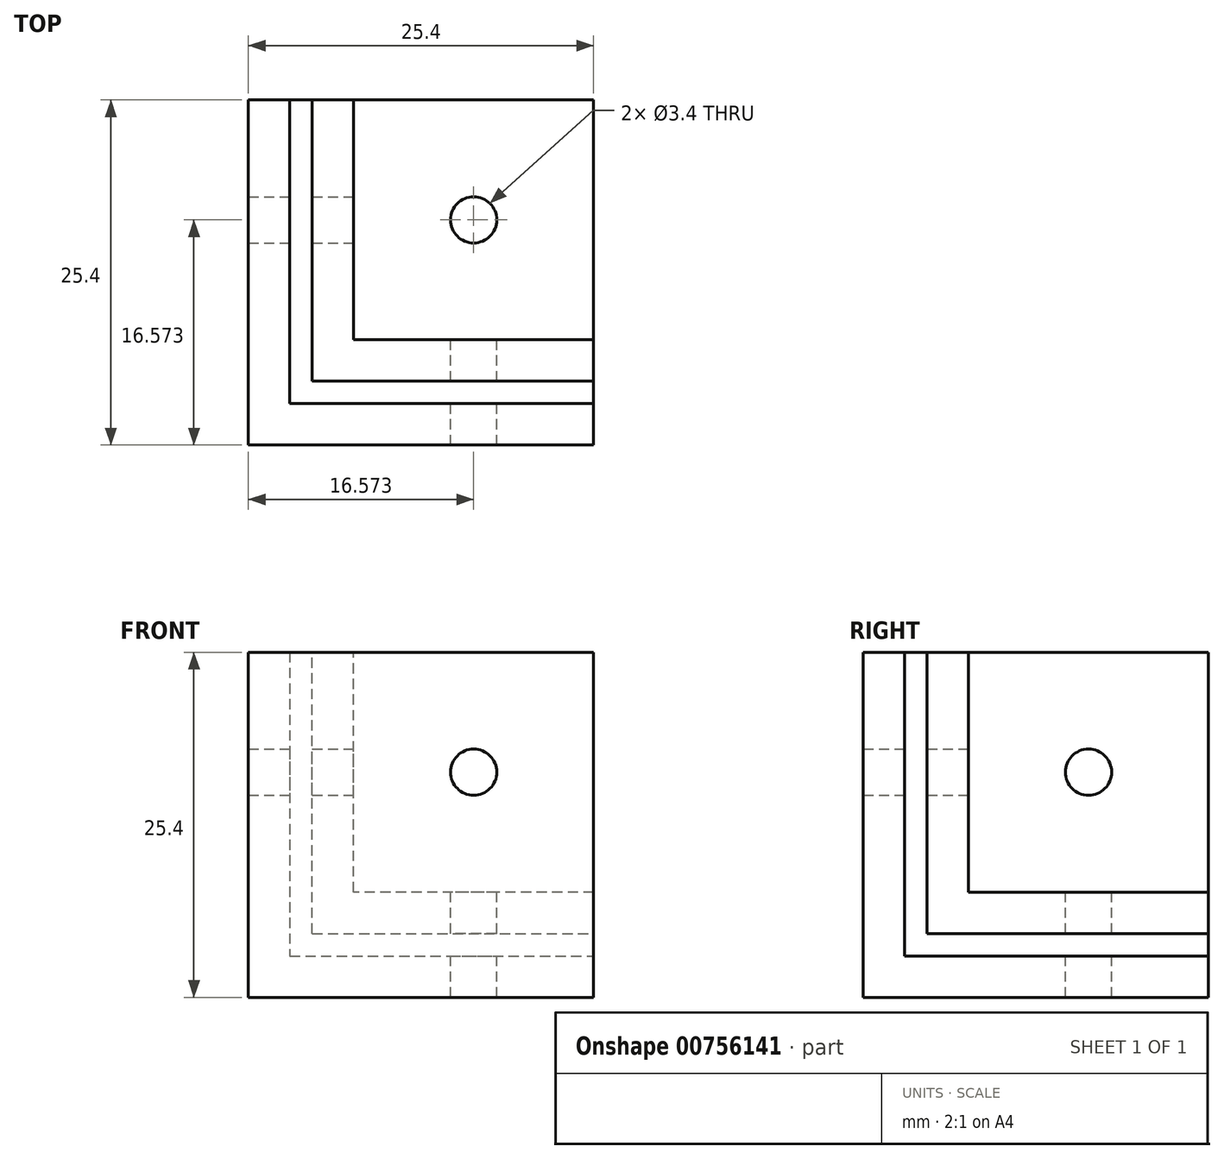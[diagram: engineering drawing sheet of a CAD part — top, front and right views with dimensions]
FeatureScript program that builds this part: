
annotation { "Feature Type Name" : "Feature", "Feature Type Description" : "" }
export const myFeature = defineFeature(function(context is Context, id is Id, definition is map)
    precondition{}
    {
        {
            var Q0;
            Q0=qCreatedBy(makeId("Front.planeOp"),FACE);
            var sketch = newSketch(context, id + "F0", { "sketchPlane" : qUnion([Q0])});
            skLineSegment(sketch, "E0.left", {"start": v(0, 0) * mm, "end": v(0, 0) * mm});
            skLineSegment(sketch, "E1.bottom", {"start": v(0, 0) * mm, "end": v(25.4, 0) * mm});
            skLineSegment(sketch, "E1.top", {"start": v(0, 25.4) * mm, "end": v(25.4, 25.4) * mm});
            skLineSegment(sketch, "E1.left", {"start": v(0, 0) * mm, "end": v(0, 25.4) * mm});
            skLineSegment(sketch, "E1.right", {"start": v(25.4, 0) * mm, "end": v(25.4, 25.4) * mm});
            skSolve(sketch);
        }
        {
            var Q0;
            Q0 = qSketchRegion(id + "F0", true);
            extrude(context, id + "F1", {"entities" : qUnion([Q0]), "depth" : 25.4 * mm, "offsetDistance" : 25.4 * mm});
        }
        {
            var Q0;
            Q0=makeQuery(id+"F1.opExtrude","CAP_FACE",FACE,{"disambiguationData":[OSD([sQuery(id+"F0.wireOp",EDGE,"E1.bottom"),sQuery(id+"F0.wireOp",EDGE,"E1.top"),sQuery(id+"F0.wireOp",EDGE,"E1.left"),sQuery(id+"F0.wireOp",EDGE,"E1.right")])],"isStart":false});
            var sketch = newSketch(context, id + "F2", { "sketchPlane" : qUnion([Q0])});
            skLineSegment(sketch, "E2", {"start": v(3.05, 3.05) * mm, "end": v(22.35, 3.05) * mm});
            skLineSegment(sketch, "E3", {"start": v(22.35, 3.05) * mm, "end": v(22.35, 4.7) * mm});
            skLineSegment(sketch, "E4", {"start": v(22.35, 4.7) * mm, "end": v(4.7, 4.7) * mm});
            skLineSegment(sketch, "E5", {"start": v(4.7, 4.7) * mm, "end": v(4.7, 22.35) * mm});
            skLineSegment(sketch, "E6", {"start": v(4.7, 22.35) * mm, "end": v(3.05, 22.35) * mm});
            skLineSegment(sketch, "E7", {"start": v(3.05, 22.35) * mm, "end": v(3.05, 3.05) * mm});
            skLineSegment(sketch, "E8", {"start": v(12.7, 3.05) * mm, "end": v(12.7, 0) * mm});
            skLineSegment(sketch, "E9", {"start": v(4.7, 22.35) * mm, "end": v(4.7, 25.4) * mm});
            skSolve(sketch);
        }
        {
            var Q0;
            Q0 = qSketchRegion(id + "F2", true);
            extrude(context, id + "F3", {"entities" : qUnion([Q0]), "operationType" : NewBodyOperationType.REMOVE, "oppositeDirection" : true, "depth" : 25.4 * mm, "offsetDistance" : 25.4 * mm});
        }
        {
            var Q0;
            Q0=makeQuery(id+"F1.opExtrude","SWEPT_FACE",FACE,{"disambiguationData":[OSD([sQuery(id+"F0.wireOp",EDGE,"E1.right")])]});
            var sketch = newSketch(context, id + "F4", { "sketchPlane" : qUnion([Q0])});
            skLineSegment(sketch, "E10", {"start": v(-22.35, 3.05) * mm, "end": v(-3.05, 3.05) * mm});
            skLineSegment(sketch, "E11", {"start": v(-3.05, 3.05) * mm, "end": v(-3.05, 4.7) * mm});
            skLineSegment(sketch, "E12", {"start": v(-3.05, 4.7) * mm, "end": v(-20.7, 4.7) * mm});
            skLineSegment(sketch, "E13", {"start": v(-20.7, 4.7) * mm, "end": v(-20.7, 22.35) * mm});
            skLineSegment(sketch, "E14", {"start": v(-20.7, 22.35) * mm, "end": v(-22.35, 22.35) * mm});
            skLineSegment(sketch, "E15", {"start": v(-22.35, 22.35) * mm, "end": v(-22.35, 3.05) * mm});
            skLineSegment(sketch, "E16", {"start": v(-12.7, 3.05) * mm, "end": v(-12.7, 0) * mm});
            skLineSegment(sketch, "E17", {"start": v(-20.7, 22.35) * mm, "end": v(-20.7, 25.4) * mm});
            skPoint(sketch, "E18", {"position": v(-12.7, 0) * mm});
            skSolve(sketch);
        }
        {
            var Q0;
            Q0 = qSketchRegion(id + "F4", true);
            extrude(context, id + "F5", {"entities" : qUnion([Q0]), "operationType" : NewBodyOperationType.REMOVE, "oppositeDirection" : true, "depth" : 25.4 * mm, "offsetDistance" : 25.4 * mm});
        }
        {
            var Q0;
            Q0=makeQuery(id+"F1.opExtrude","SWEPT_FACE",FACE,{"disambiguationData":[OSD([sQuery(id+"F0.wireOp",EDGE,"E1.top")])]});
            var sketch = newSketch(context, id + "F6", { "sketchPlane" : qUnion([Q0])});
            skLineSegment(sketch, "E19", {"start": v(3.05, -22.35) * mm, "end": v(22.35, -22.35) * mm});
            skLineSegment(sketch, "E20", {"start": v(22.35, -22.35) * mm, "end": v(22.35, -20.7) * mm});
            skLineSegment(sketch, "E21", {"start": v(22.35, -20.7) * mm, "end": v(4.7, -20.7) * mm});
            skLineSegment(sketch, "E22", {"start": v(4.7, -20.7) * mm, "end": v(4.7, -3.05) * mm});
            skLineSegment(sketch, "E23", {"start": v(4.7, -3.05) * mm, "end": v(3.05, -3.05) * mm});
            skLineSegment(sketch, "E24", {"start": v(3.05, -3.05) * mm, "end": v(3.05, -22.35) * mm});
            skLineSegment(sketch, "E25", {"start": v(12.7, -22.35) * mm, "end": v(12.7, -25.4) * mm});
            skLineSegment(sketch, "E26", {"start": v(4.7, -3.05) * mm, "end": v(4.7, 0) * mm});
            skSolve(sketch);
        }
        {
            var Q0;
            Q0 = qSketchRegion(id + "F6", true);
            extrude(context, id + "F7", {"entities" : qUnion([Q0]), "operationType" : NewBodyOperationType.REMOVE, "oppositeDirection" : true, "depth" : 25.4 * mm, "offsetDistance" : 25.4 * mm});
        }
        {
            var Q0;
            Q0=makeQuery(id+"F1.opExtrude","CAP_FACE",FACE,{"disambiguationData":[OSD([sQuery(id+"F0.wireOp",EDGE,"E1.bottom"),sQuery(id+"F0.wireOp",EDGE,"E1.top"),sQuery(id+"F0.wireOp",EDGE,"E1.left"),sQuery(id+"F0.wireOp",EDGE,"E1.right")])],"isStart":true});
            var sketch = newSketch(context, id + "F8", { "sketchPlane" : qUnion([Q0])});
            skLineSegment(sketch, "E27.bottom", {"start": v(-3.05, 0) * mm, "end": v(0, 0) * mm});
            skLineSegment(sketch, "E27.top", {"start": v(-3.05, 25.4) * mm, "end": v(0, 25.4) * mm});
            skLineSegment(sketch, "E27.left", {"start": v(-3.05, 0) * mm, "end": v(-3.05, 25.4) * mm});
            skLineSegment(sketch, "E27.right", {"start": v(0, 0) * mm, "end": v(0, 25.4) * mm});
            skLineSegment(sketch, "E28.bottom", {"start": v(0, 0) * mm, "end": v(-25.4, 0) * mm});
            skLineSegment(sketch, "E28.top", {"start": v(0, 3.05) * mm, "end": v(-25.4, 3.05) * mm});
            skLineSegment(sketch, "E28.left", {"start": v(0, 0) * mm, "end": v(0, 3.05) * mm});
            skLineSegment(sketch, "E28.right", {"start": v(-25.4, 0) * mm, "end": v(-25.4, 3.05) * mm});
            skSolve(sketch);
        }
        {
            var Q0;
            Q0 = qSketchRegion(id + "F8", true);
            extrude(context, id + "F9", {"entities" : qUnion([Q0]), "operationType" : NewBodyOperationType.ADD, "oppositeDirection" : true, "depth" : 25.4 * mm, "offsetDistance" : 25.4 * mm});
        }
        {
            var Q0;
            Q0=makeQuery(id+"F1.opExtrude","SWEPT_FACE",FACE,{"disambiguationData":[OSD([sQuery(id+"F0.wireOp",EDGE,"E1.right")])]});
            var sketch = newSketch(context, id + "F10", { "sketchPlane" : qUnion([Q0])});
            skLineSegment(sketch, "E29.bottom", {"start": v(-22.35, 0) * mm, "end": v(-25.4, 0) * mm});
            skLineSegment(sketch, "E29.top", {"start": v(-22.35, 25.4) * mm, "end": v(-25.4, 25.4) * mm});
            skLineSegment(sketch, "E29.left", {"start": v(-22.35, 0) * mm, "end": v(-22.35, 25.4) * mm});
            skLineSegment(sketch, "E29.right", {"start": v(-25.4, 0) * mm, "end": v(-25.4, 25.4) * mm});
            skSolve(sketch);
        }
        {
            var Q0;
            Q0 = qSketchRegion(id + "F10", true);
            extrude(context, id + "F11", {"entities" : qUnion([Q0]), "operationType" : NewBodyOperationType.ADD, "oppositeDirection" : true, "depth" : 25.4 * mm, "offsetDistance" : 25.4 * mm});
        }
        {
            var Q0;
            Q0=makeQuery(id+"F1.opExtrude","SWEPT_FACE",FACE,{"disambiguationData":[OSD([sQuery(id+"F0.wireOp",EDGE,"E1.top")])]});
            var sketch = newSketch(context, id + "F12", { "sketchPlane" : qUnion([Q0])});
            skLineSegment(sketch, "E30.bottom", {"start": v(25.4, 0) * mm, "end": v(7.75, 0) * mm});
            skLineSegment(sketch, "E30.top", {"start": v(25.4, -17.65) * mm, "end": v(7.75, -17.65) * mm});
            skLineSegment(sketch, "E30.left", {"start": v(25.4, 0) * mm, "end": v(25.4, -17.65) * mm});
            skLineSegment(sketch, "E30.right", {"start": v(7.75, 0) * mm, "end": v(7.75, -17.65) * mm});
            skSolve(sketch);
        }
        {
            var Q0;
            Q0 = qSketchRegion(id + "F12", true);
            extrude(context, id + "F13", {"entities" : qUnion([Q0]), "operationType" : NewBodyOperationType.REMOVE, "oppositeDirection" : true, "depth" : 17.65 * mm, "offsetDistance" : 25.4 * mm});
        }
        {
            var Q0;
            Q0=makeQuery(id+"F1.opExtrude","SWEPT_FACE",FACE,{"disambiguationData":[OSD([sQuery(id+"F0.wireOp",EDGE,"E1.top")])]});
            var sketch = newSketch(context, id + "F14", { "sketchPlane" : qUnion([Q0])});
            skLineSegment(sketch, "E31.bottom", {"start": v(3.05, -3.05) * mm, "end": v(4.7, -3.05) * mm});
            skLineSegment(sketch, "E31.top", {"start": v(3.05, 0) * mm, "end": v(4.7, 0) * mm});
            skLineSegment(sketch, "E31.left", {"start": v(3.05, -3.05) * mm, "end": v(3.05, 0) * mm});
            skLineSegment(sketch, "E31.right", {"start": v(4.7, -3.05) * mm, "end": v(4.7, 0) * mm});
            skLineSegment(sketch, "E32.bottom", {"start": v(22.35, -22.35) * mm, "end": v(25.4, -22.35) * mm});
            skLineSegment(sketch, "E32.top", {"start": v(22.35, -20.7) * mm, "end": v(25.4, -20.7) * mm});
            skLineSegment(sketch, "E32.left", {"start": v(22.35, -22.35) * mm, "end": v(22.35, -20.7) * mm});
            skLineSegment(sketch, "E32.right", {"start": v(25.4, -22.35) * mm, "end": v(25.4, -20.7) * mm});
            skSolve(sketch);
        }
        {
            var Q0;
            Q0 = qSketchRegion(id + "F14", true);
            var Q1;
            {var subQ1=makeQuery(id+"F5.opExtrude","SWEPT_FACE",FACE,{"disambiguationData":[OSD([sQuery(id+"F4.wireOp",EDGE,"E10")])]});var subQ4=makeQuery(id+"F3.boolean.opBoolean","COPY",FACE,{"derivedFrom":makeQuery(id+"F3.opExtrude","SWEPT_FACE",FACE,{"disambiguationData":[OSD([sQuery(id+"F2.wireOp",EDGE,"E2")])]})});var subQ5=sQuery(id+"F0.wireOp",EDGE,"E1.left");var subQ9=sQuery(id+"F0.wireOp",EDGE,"E1.right");var subQ10=makeQuery(id+"F1.opExtrude","SWEPT_FACE",FACE,{"disambiguationData":[OSD([subQ9])]});var subQ12=sQuery(id+"F0.wireOp",EDGE,"E1.top");var subQ13=sQuery(id+"F0.wireOp",EDGE,"E1.bottom");var subQ20=makeQuery(id+"F5.boolean.opBoolean","MERGE",FACE,{"derivedFrom":[subQ4,subQ1]});Q1=makeQuery(id+"F9.boolean.opBoolean","MERGE",FACE,{"derivedFrom":[makeQuery(id+"F7.boolean.opBoolean","SPLIT",FACE,{"disambiguationData":[TD([makeQuery(id+"F1.opExtrude","CAP_FACE",FACE,{"disambiguationData":[OSD([subQ13,subQ12,subQ5,subQ9])],"isStart":false})])],"derivedFrom":subQ20}),makeQuery(id+"F7.boolean.opBoolean","SPLIT",FACE,{"disambiguationData":[TD([subQ10])],"derivedFrom":subQ20}),makeQuery(id+"F9.opExtrude","SWEPT_FACE",FACE,{"disambiguationData":[OSD([sQuery(id+"F8.wireOp",EDGE,"E28.top")])]})]});}
            extrude(context, id + "F15", {"entities" : qUnion([Q0]), "operationType" : NewBodyOperationType.REMOVE, "endBound" : BoundingType.UP_TO_SURFACE, "oppositeDirection" : true, "depth" : 25.4 * mm, "endBoundEntityFace" : qUnion([Q1]), "offsetDistance" : 25.4 * mm});
        }
        {
            var Q0;
            Q0=makeQuery(id+"F1.opExtrude","SWEPT_FACE",FACE,{"disambiguationData":[OSD([sQuery(id+"F0.wireOp",EDGE,"E1.right")])]});
            var sketch = newSketch(context, id + "F16", { "sketchPlane" : qUnion([Q0])});
            skLineSegment(sketch, "E33.bottom", {"start": v(-3.05, 4.7) * mm, "end": v(0, 4.7) * mm});
            skLineSegment(sketch, "E33.top", {"start": v(-3.05, 3.05) * mm, "end": v(0, 3.05) * mm});
            skLineSegment(sketch, "E33.left", {"start": v(-3.05, 4.7) * mm, "end": v(-3.05, 3.05) * mm});
            skLineSegment(sketch, "E33.right", {"start": v(0, 4.7) * mm, "end": v(0, 3.05) * mm});
            skSolve(sketch);
        }
        {
            var Q0;
            Q0 = qSketchRegion(id + "F16", true);
            var Q1;
            {var subQ8=makeQuery(id+"F3.boolean.opBoolean","COPY",FACE,{"derivedFrom":makeQuery(id+"F3.opExtrude","SWEPT_FACE",FACE,{"disambiguationData":[OSD([sQuery(id+"F2.wireOp",EDGE,"E7")])]})});Q1=makeQuery(id+"F15.boolean.opBoolean","MERGE",FACE,{"derivedFrom":[makeQuery(id+"F9.boolean.opBoolean","MERGE",FACE,{"derivedFrom":[makeQuery(id+"F5.boolean.opBoolean","SPLIT",FACE,{"disambiguationData":[TD([makeQuery(id+"F5.opExtrude","SWEPT_FACE",FACE,{"disambiguationData":[OSD([sQuery(id+"F4.wireOp",EDGE,"E15")])]})])],"derivedFrom":subQ8}),makeQuery(id+"F7.boolean.opBoolean","MERGE",FACE,{"derivedFrom":[makeQuery(id+"F5.boolean.opBoolean","SPLIT",FACE,{"disambiguationData":[TD([makeQuery(id+"F5.opExtrude","SWEPT_FACE",FACE,{"disambiguationData":[OSD([sQuery(id+"F4.wireOp",EDGE,"E11")])]})])],"derivedFrom":subQ8}),makeQuery(id+"F7.opExtrude","SWEPT_FACE",FACE,{"disambiguationData":[OSD([sQuery(id+"F6.wireOp",EDGE,"E24")])]})]}),makeQuery(id+"F9.opExtrude","SWEPT_FACE",FACE,{"disambiguationData":[OSD([sQuery(id+"F8.wireOp",EDGE,"E27.left")])]})]}),makeQuery(id+"F15.opExtrude","SWEPT_FACE",FACE,{"disambiguationData":[OSD([sQuery(id+"F14.wireOp",EDGE,"E31.left")])]})]});}
            extrude(context, id + "F17", {"entities" : qUnion([Q0]), "operationType" : NewBodyOperationType.REMOVE, "endBound" : BoundingType.UP_TO_SURFACE, "oppositeDirection" : true, "depth" : 25.4 * mm, "endBoundEntityFace" : qUnion([Q1]), "offsetDistance" : 25.4 * mm});
        }
        {
            var Q0;
            Q0=makeQuery(id+"F13.boolean.opBoolean","COPY",FACE,{"derivedFrom":makeQuery(id+"F13.opExtrude","SWEPT_FACE",FACE,{"disambiguationData":[OSD([sQuery(id+"F12.wireOp",EDGE,"E30.top")])]})});
            var sketch = newSketch(context, id + "F18", { "sketchPlane" : qUnion([Q0])});
            skCircle(sketch, "E34", {"center": v(-16.57, 16.57) * mm, "radius": 1.7 * mm});
            skPoint(sketch, "E34.centerSnap0", {"position": v(-25.4, 16.57) * mm});
            skPoint(sketch, "E34.centerSnap1", {"position": v(-16.57, 25.4) * mm});
            skSolve(sketch);
        }
        {
            var Q0;
            Q0 = qSketchRegion(id + "F18", true);
            extrude(context, id + "F19", {"entities" : qUnion([Q0]), "operationType" : NewBodyOperationType.REMOVE, "oppositeDirection" : true, "depth" : 25.4 * mm, "offsetDistance" : 25.4 * mm});
        }
        {
            var Q0;
            Q0=makeQuery(id+"F13.boolean.opBoolean","COPY",FACE,{"derivedFrom":makeQuery(id+"F13.opExtrude","SWEPT_FACE",FACE,{"disambiguationData":[OSD([sQuery(id+"F12.wireOp",EDGE,"E30.right")])]})});
            var sketch = newSketch(context, id + "F20", { "sketchPlane" : qUnion([Q0])});
            skCircle(sketch, "E35", {"center": v(-8.83, 16.57) * mm, "radius": 1.7 * mm});
            skPoint(sketch, "E35.centerSnap0", {"position": v(0, 16.57) * mm});
            skPoint(sketch, "E35.centerSnap1", {"position": v(-8.83, 25.4) * mm});
            skSolve(sketch);
        }
        {
            var Q0;
            Q0=makeQuery(id+"F20.imprint","IMPRINT",FACE,{"disambiguationData":[TD([[makeQuery(id+"F20.imprint","IMPRINT",EDGE,{"derivedFrom":sQuery(id+"F20.wireOp",EDGE,"E35")}),1.0]])]});
            extrude(context, id + "F21", {"entities" : qUnion([Q0]), "operationType" : NewBodyOperationType.REMOVE, "oppositeDirection" : true, "depth" : 25.4 * mm, "offsetDistance" : 25.4 * mm});
        }
        {
            var Q0;
            Q0=makeQuery(id+"F13.boolean.opBoolean","COPY",FACE,{"derivedFrom":makeQuery(id+"F13.opExtrude","CAP_FACE",FACE,{"disambiguationData":[OSD([sQuery(id+"F12.wireOp",EDGE,"E30.bottom"),sQuery(id+"F12.wireOp",EDGE,"E30.top"),sQuery(id+"F12.wireOp",EDGE,"E30.left"),sQuery(id+"F12.wireOp",EDGE,"E30.right")])],"isStart":false})});
            var sketch = newSketch(context, id + "F22", { "sketchPlane" : qUnion([Q0])});
            skCircle(sketch, "E36", {"center": v(16.57, -8.83) * mm, "radius": 1.7 * mm});
            skPoint(sketch, "E36.centerSnap0", {"position": v(25.4, -8.83) * mm});
            skPoint(sketch, "E36.centerSnap1", {"position": v(16.57, 0) * mm});
            skSolve(sketch);
        }
        {
            var Q0;
            Q0 = qSketchRegion(id + "F22", true);
            extrude(context, id + "F23", {"entities" : qUnion([Q0]), "operationType" : NewBodyOperationType.REMOVE, "oppositeDirection" : true, "depth" : 25.4 * mm, "offsetDistance" : 25.4 * mm});
        }
        {
            var Q0;
            Q0=makeQuery(id+"F13.boolean.opBoolean","COPY",FACE,{"derivedFrom":makeQuery(id+"F13.opExtrude","SWEPT_FACE",FACE,{"disambiguationData":[OSD([sQuery(id+"F12.wireOp",EDGE,"E30.top")])]})});
            var sketch = newSketch(context, id + "F24", { "sketchPlane" : qUnion([Q0])});
            skCircle(sketch, "E37", {"center": v(-16.57, 16.57) * mm, "radius": 1.7 * mm});
            skSolve(sketch);
        }
        {
            var Q0;
            Q0 = qSketchRegion(id + "F24", true);
            extrude(context, id + "F25", {"entities" : qUnion([Q0]), "operationType" : NewBodyOperationType.REMOVE, "oppositeDirection" : true, "depth" : 25.4 * mm, "offsetDistance" : 25.4 * mm});
        }
    });
